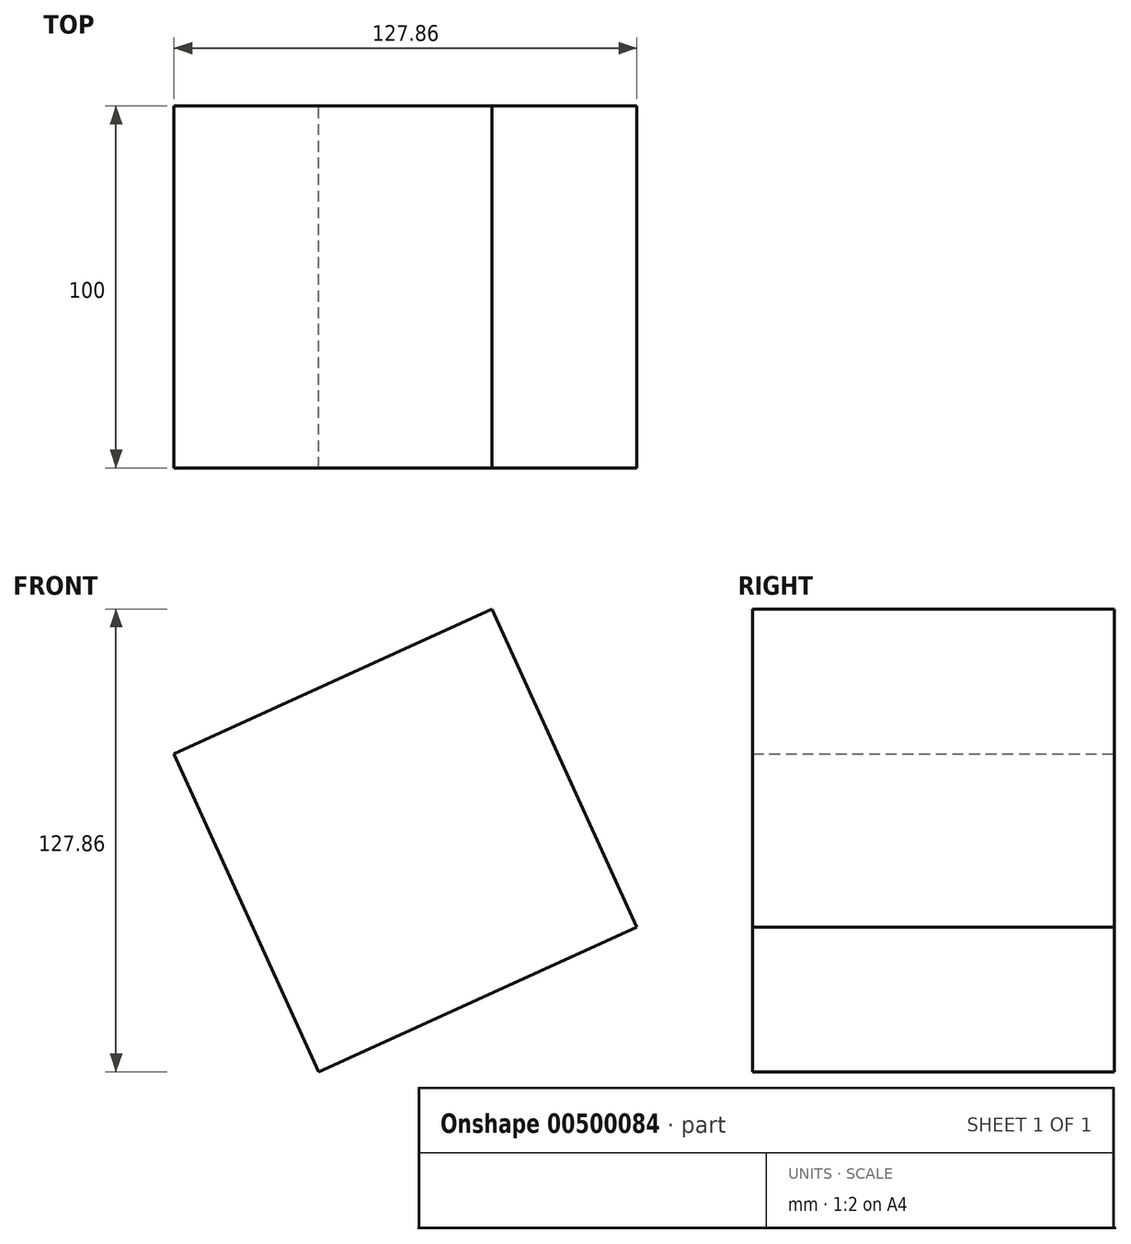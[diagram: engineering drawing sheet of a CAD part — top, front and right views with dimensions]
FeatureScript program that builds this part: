
annotation { "Feature Type Name" : "Feature", "Feature Type Description" : "" }
export const myFeature = defineFeature(function(context is Context, id is Id, definition is map)
    precondition{}
    {
        {
            var Q0;
            Q0=qCreatedBy(makeId("Front.planeOp"),FACE);
            var sketch = newSketch(context, id + "F0", { "sketchPlane" : qUnion([Q0])});
            skCircle(sketch, "E0.cCircle", {"center": v(0, -3.48) * mm, "radius": 68.26 * mm, "construction": true});
            skLineSegment(sketch, "E0.0", {"start": v(63.93, -27.4) * mm, "end": v(-23.92, -67.4) * mm});
            skLineSegment(sketch, "E0.1", {"start": v(-23.92, -67.4) * mm, "end": v(-63.93, 20.44) * mm});
            skLineSegment(sketch, "E0.2", {"start": v(-63.93, 20.44) * mm, "end": v(23.92, 60.45) * mm});
            skLineSegment(sketch, "E0.3", {"start": v(23.92, 60.45) * mm, "end": v(63.93, -27.4) * mm});
            skSolve(sketch);
        }
        {
            var Q0;
            Q0=makeQuery(id+"F0.imprint","IMPRINT",FACE,{"disambiguationData":[TD([[makeQuery(id+"F0.imprint","IMPRINT",EDGE,{"derivedFrom":sQuery(id+"F0.wireOp",EDGE,"E0.0")}),-1.0]])]});
            extrude(context, id + "F1", {"entities" : qUnion([Q0]), "endBound" : BoundingType.SYMMETRIC, "depth" : 100 * mm});
        }
    });
